# Revit family: LG_Heat_Pump_Water_Heater_APHWC801L_NA_v1.1
name_source: partatom
category: Mechanical Equipment
units: mm (PartAtom-declared; Revit-internal decimal feet)

## family parameters
Always vertical = Yes
Classification = None
Cut with Voids When Loaded = No
Part Type = Normal
Room Calculation Point = No
Round Connector Dimension = Use Diameter
Shared = No
Work Plane-Based = No

## types (1)
- APHWC801L
    Annual Energy Consumption(AEC) (15C / 7C)_kWH = -
    Anode = Sacrificial
    Available Voltage Range_V = -
    Buyer Model = APHWC801L
    Capacity_Volume_L = 303 (80 gal)
    Circuit Breaker_A = 30.1
    Compressor_Manufacturer = -
    Compressor_Type = Twin Rotary
    Default Elevation = 0"
    Defrost Method = Reverse Cycle
    Description = HEAT PUMP WATER HEATER
    Drain Hose Size_I.D_in = 3/4 (1/2)
    Drain Hose Size_I.D_mm = -
    Energy_FHR_Gallon/hour = 94
    Energy_UEF = 3.9
    Factory Model = APHWC801L
    Foam Insulation_mm = 40 ~ 80 / 1.6 ~ 2.4 inch
    Indoor_Air Flow Rate_CFM = -
    Indoor_Air Flow Rate_m3/min = -
    Indoor_Dimensions_Net (W x H x D)_in = 22-27/32 x 79-1/16 x 22-29/32
    Indoor_Dimensions_Net (W x H x D)_mm = -
    Indoor_Exterior Color Code = Luxury Silver
    Indoor_Heat Pump Operation Range_C(DB) = -
    Indoor_Heat Pump Operation Range_F(DB) = 23 ~ 120
    Indoor_Max. Fuse Size_A = -
    Indoor_Sound Power Level_dB(A) = -
    Indoor_Sound Pressure Level_dB(A) = 42
    Indoor_Weight_Net_kg = -
    Indoor_Weight_Net_lb = 264
    Manufacturer = LG Electronics
    Max Working Pressure (Water Tank)_PSI = 150
    Max Working Pressure (Water Tank)_kPa = -
    Power Input_Lower Element_W = 3800 (208 V) / 5000 (240 V)
    Power Input_Upper Element_W = 3800 (208 V) / 5000 (240 V)
    Power Supply Cable_AWG = 10
    Power Supply Cable_No. = 3
    Power Supply_Ø_V_Hz = 1, 208 / 240, 60
    Refrigerant_GWP = -
    Refrigerant_Pre Charge_g = -
    Refrigerant_Pre Charge_oz = 26
    Refrigerant_Pre Charge_t-Co2 eq = -
    Refrigerant_Type = R134a
    Water Connection Size_inch = 3/4
